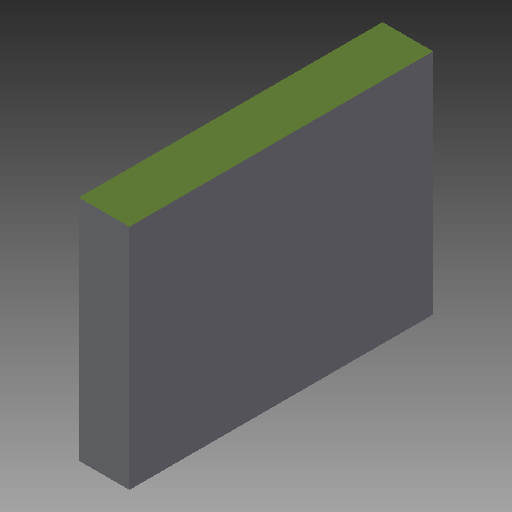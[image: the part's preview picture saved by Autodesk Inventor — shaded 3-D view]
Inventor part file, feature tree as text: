
AUTODESK INVENTOR PART (.ipt)
format: ipt  version: 2017 (Build 210142000, 142)  size: 108,032 bytes
history: native  units: in
note: dims shown in document units (in); Inventor stores cm internally (conversion verified against a paired STEP export)
features: extrude x1, sketch x1
ambient origin geometry x8: Origin, YZ Plane, XZ Plane, XY Plane, X Axis, Y Axis, Z Axis, Center Point
bodies: Solid1 (feature_tree)
feature tree (2):
  extrude  "Extrusion1"  Depth=9.0in
  sketch  "Sketch1"  dims[d0=12.0in d1=9.0in d2=2.0in d3=0.0in]
